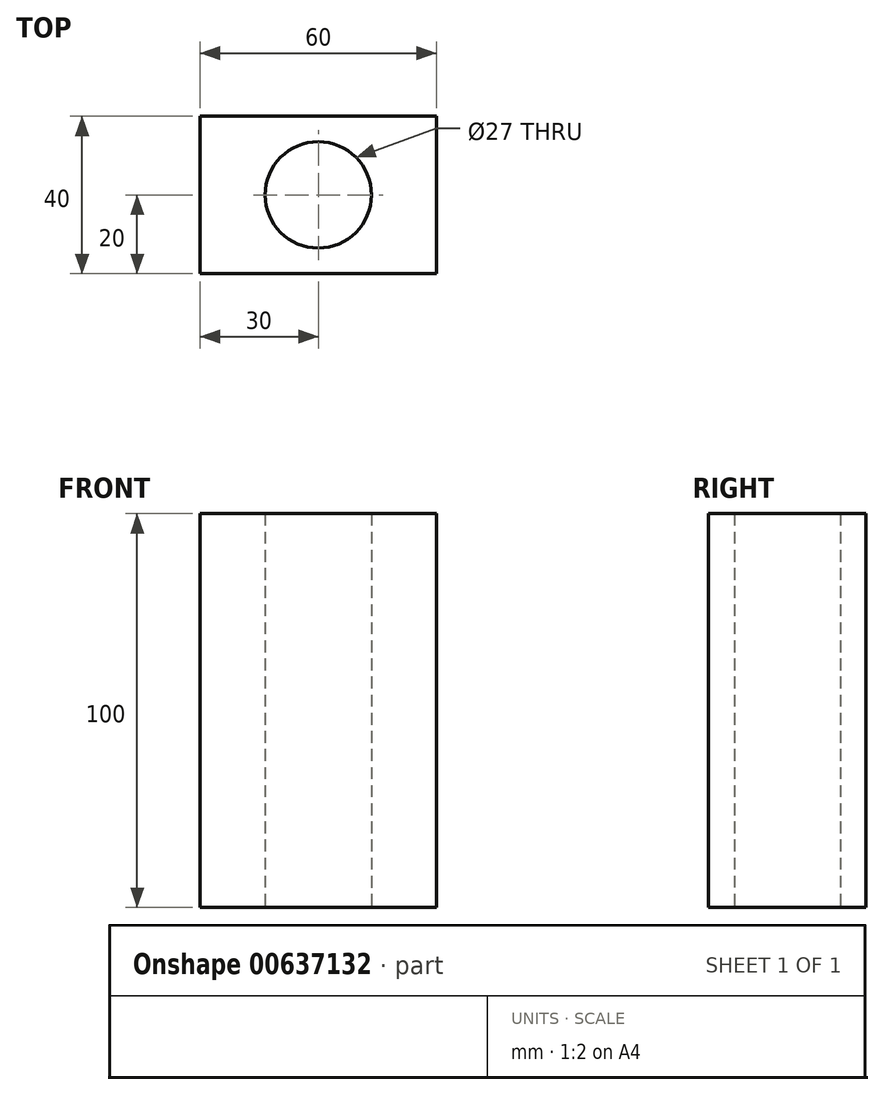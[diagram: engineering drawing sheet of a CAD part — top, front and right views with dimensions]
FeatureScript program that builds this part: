
annotation { "Feature Type Name" : "Feature", "Feature Type Description" : "" }
export const myFeature = defineFeature(function(context is Context, id is Id, definition is map)
    precondition{}
    {
        {
            var Q0;
            Q0=qCreatedBy(makeId("Top.planeOp"),FACE);
            var sketch = newSketch(context, id + "F0", { "sketchPlane" : qUnion([Q0])});
            skCircle(sketch, "E0", {"center": v(0, 0) * mm, "radius": 13.5 * mm});
            skLineSegment(sketch, "E1.bottom", {"start": v(-30, 20) * mm, "end": v(30, 20) * mm});
            skLineSegment(sketch, "E1.top", {"start": v(-30, -20) * mm, "end": v(30, -20) * mm});
            skLineSegment(sketch, "E1.left", {"start": v(-30, 20) * mm, "end": v(-30, -20) * mm});
            skLineSegment(sketch, "E1.right", {"start": v(30, 20) * mm, "end": v(30, -20) * mm});
            skSolve(sketch);
        }
        {
            var Q0;
            Q0=makeQuery(id+"F0.imprint","IMPRINT",FACE,{"disambiguationData":[TD([[makeQuery(id+"F0.imprint","IMPRINT",EDGE,{"derivedFrom":sQuery(id+"F0.wireOp",EDGE,"E0")}),-1.0]])]});
            extrude(context, id + "F1", {"entities" : qUnion([Q0]), "endBound" : BoundingType.SYMMETRIC, "depth" : 100 * mm, "offsetDistance" : 25 * mm});
        }
    });
